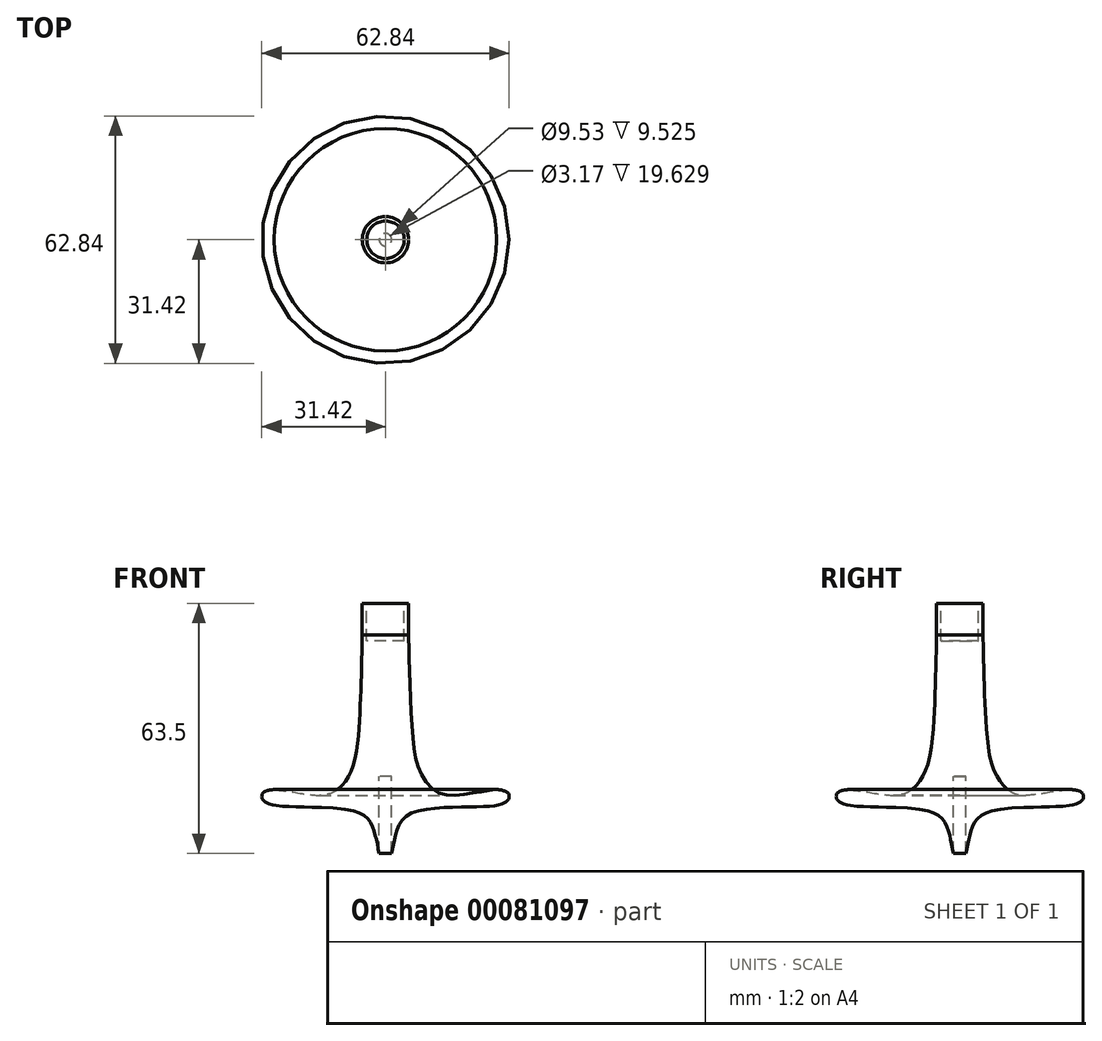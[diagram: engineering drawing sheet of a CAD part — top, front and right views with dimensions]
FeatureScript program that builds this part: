
annotation { "Feature Type Name" : "Feature", "Feature Type Description" : "" }
export const myFeature = defineFeature(function(context is Context, id is Id, definition is map)
    precondition{}
    {
        {
            var Q0;
            Q0=qCreatedBy(makeId("Front.planeOp"),FACE);
            var sketch = newSketch(context, id + "F0", { "sketchPlane" : qUnion([Q0])});
            skLineSegment(sketch, "E0", {"start": v(0, 0) * mm, "end": v(31.75, 0) * mm});
            skFitSpline(sketch, "E1", {"points": [v(1.59, -12.96) * mm, v(2.53, -8.6) * mm, v(5.32, -3.4) * mm, v(18.39, -1.2) * mm, v(27.76, -0.81) * mm, v(30.36, 0) * mm, v(31.36, 1.08) * mm, v(31.26, 2.18) * mm, v(30.56, 2.78) * mm, v(29.16, 3.18) * mm, v(28.26, 3.28) * mm, v(28.16, 3.28) * mm], "startDerivative": vector(7.51, 36.72) * mm, "endDerivative": vector(-4.46, -0.16) * mm});
            skLineSegment(sketch, "E2", {"start": v(4.76, 50.54) * mm, "end": v(4.76, 41.01) * mm});
            skLineSegment(sketch, "E3", {"start": v(4.76, 41.01) * mm, "end": v(0, 41.01) * mm});
            skLineSegment(sketch, "E4", {"start": v(4.76, 50.54) * mm, "end": v(5.89, 50.54) * mm});
            skLineSegment(sketch, "E5", {"start": v(5.89, 50.54) * mm, "end": v(5.89, 41) * mm});
            skFitSpline(sketch, "E6", {"points": [v(28.26, 3.28) * mm, v(21.36, 2.3) * mm, v(13.83, 2.3) * mm, v(8.98, 7.51) * mm, v(6.91, 16.74) * mm, v(6.06, 35.19) * mm, v(5.89, 42.6) * mm, v(5.89, 42.72) * mm], "startDerivative": vector(-46.85, -6.39) * mm, "endDerivative": vector(0.06, 4.17) * mm});
            skLineSegment(sketch, "E7", {"start": v(1.59, -12.96) * mm, "end": v(1.59, 6.67) * mm});
            skLineSegment(sketch, "E8", {"start": v(1.59, 6.67) * mm, "end": v(0, 6.67) * mm});
            skLineSegment(sketch, "E9", {"start": v(0, 41.01) * mm, "end": v(0, 6.67) * mm});
            skSolve(sketch);
        }
        {
            var Q0;
            Q0 = qSketchRegion(id + "F0", true);
            var Q1;
            Q1=sQuery(id+"F0.wireOp",EDGE,"E9");
            revolve(context, id + "F1", {"entities" : qUnion([Q0]), "axis" : qUnion([Q1]), "revolveType" : RevolveType.FULL});
        }
    });
